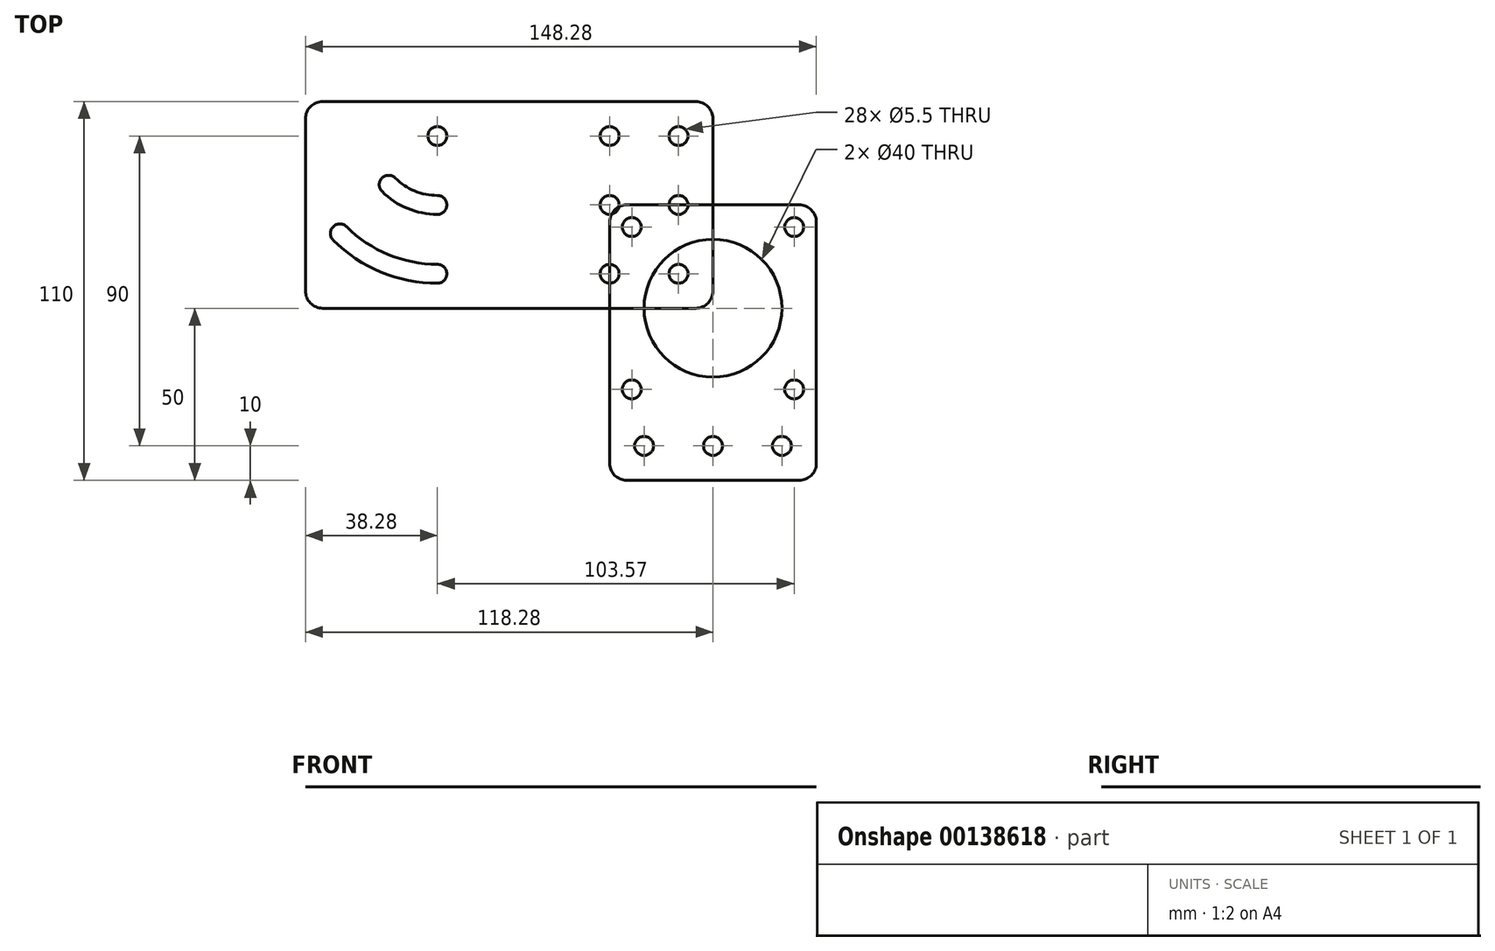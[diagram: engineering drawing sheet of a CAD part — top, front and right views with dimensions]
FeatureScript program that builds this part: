
annotation { "Feature Type Name" : "Feature", "Feature Type Description" : "" }
export const myFeature = defineFeature(function(context is Context, id is Id, definition is map)
    precondition{}
    {
        {
            var Q0;
            Q0=qCreatedBy(makeId("Top.planeOp"),FACE);
            var sketch = newSketch(context, id + "F0", { "sketchPlane" : qUnion([Q0])});
            skCircle(sketch, "E0", {"center": v(0, 0) * mm, "radius": 20 * mm});
            skLineSegment(sketch, "E1", {"start": v(-30, -30) * mm, "end": v(30, -30) * mm, "construction": true});
            skLineSegment(sketch, "E2", {"start": v(30, -30) * mm, "end": v(30, 25) * mm});
            skPoint(sketch, "E3", {"position": v(30, 0) * mm});
            skPoint(sketch, "E4", {"position": v(0, -30) * mm});
            skLineSegment(sketch, "E5", {"start": v(-30, 0) * mm, "end": v(30, 0) * mm, "construction": true});
            skLineSegment(sketch, "E6", {"start": v(0, 30) * mm, "end": v(0, -30) * mm, "construction": true});
            skLineSegment(sketch, "E7", {"start": v(25, 30) * mm, "end": v(-25, 30) * mm});
            skLineSegment(sketch, "E8", {"start": v(-30, 25) * mm, "end": v(-30, -30) * mm});
            skLineSegment(sketch, "E9", {"start": v(-23.57, 23.57) * mm, "end": v(23.57, 23.57) * mm, "construction": true});
            skPoint(sketch, "E10", {"position": v(0, 23.57) * mm});
            skLineSegment(sketch, "E11", {"start": v(23.57, 23.57) * mm, "end": v(23.57, -23.57) * mm, "construction": true});
            skPoint(sketch, "E12", {"position": v(23.57, 0) * mm});
            skLineSegment(sketch, "E13", {"start": v(-23.57, 23.57) * mm, "end": v(-23.57, -23.57) * mm, "construction": true});
            skLineSegment(sketch, "E14", {"start": v(-23.57, -23.57) * mm, "end": v(23.57, -23.57) * mm, "construction": true});
            skCircle(sketch, "E15", {"center": v(-23.57, 23.57) * mm, "radius": 2.75 * mm});
            skCircle(sketch, "E16", {"center": v(23.57, 23.57) * mm, "radius": 2.75 * mm});
            skCircle(sketch, "E17", {"center": v(-23.57, -23.57) * mm, "radius": 2.75 * mm});
            skCircle(sketch, "E18", {"center": v(23.57, -23.57) * mm, "radius": 2.75 * mm});
            skLineSegment(sketch, "E19", {"start": v(-30, -30) * mm, "end": v(-30, -45) * mm});
            skLineSegment(sketch, "E20", {"start": v(-25, -50) * mm, "end": v(25, -50) * mm});
            skLineSegment(sketch, "E21", {"start": v(30, -45) * mm, "end": v(30, -30) * mm});
            skLineSegment(sketch, "E22", {"start": v(-30, -40) * mm, "end": v(30, -40) * mm, "construction": true});
            skLineSegment(sketch, "E23", {"start": v(0, -30) * mm, "end": v(0, -50) * mm, "construction": true});
            skPoint(sketch, "E24", {"position": v(0, -40) * mm});
            skPoint(sketch, "E25", {"position": v(-20, -40) * mm});
            skPoint(sketch, "E26", {"position": v(20, -40) * mm});
            skCircle(sketch, "E27", {"center": v(-20, -40) * mm, "radius": 2.75 * mm});
            skCircle(sketch, "E28", {"center": v(0, -40) * mm, "radius": 2.75 * mm});
            skCircle(sketch, "E29", {"center": v(20, -40) * mm, "radius": 2.75 * mm});
            skPoint(sketch, "E30.visualSharp", {"position": v(-30, 30) * mm});
            skArc(sketch, "E30.filletArc", {"start": v(-25, 30) * mm, "mid": v(-28.54, 28.54) * mm, "end": v(-30, 25) * mm});
            skPoint(sketch, "E31.visualSharp", {"position": v(-30, -50) * mm});
            skArc(sketch, "E31.filletArc", {"start": v(-30, -45) * mm, "mid": v(-28.54, -48.54) * mm, "end": v(-25, -50) * mm});
            skPoint(sketch, "E32.visualSharp", {"position": v(30, -50) * mm});
            skArc(sketch, "E32.filletArc", {"start": v(25, -50) * mm, "mid": v(28.54, -48.54) * mm, "end": v(30, -45) * mm});
            skPoint(sketch, "E33.visualSharp", {"position": v(30, 30) * mm});
            skArc(sketch, "E33.filletArc", {"start": v(30, 25) * mm, "mid": v(28.54, 28.54) * mm, "end": v(25, 30) * mm});
            skSolve(sketch);
        }
        {
            var Q0;
            Q0=makeQuery(id+"F0.imprint","IMPRINT",FACE,{"disambiguationData":[TD([[makeQuery(id+"F0.imprint","IMPRINT",EDGE,{"derivedFrom":sQuery(id+"F0.wireOp",EDGE,"E0")}),-1.0]])]});
            extrude(context, id + "F1", {"entities" : qUnion([Q0]), "depth" : 1 / 203.2 * mm});
        }
        {
            var Q0;
            Q0=qCreatedBy(makeId("Top.planeOp"),FACE);
            var sketch = newSketch(context, id + "F2", { "sketchPlane" : qUnion([Q0])});
            skLineSegment(sketch, "E34.bottom", {"start": v(-5, 0) * mm, "end": v(-113.28, 0) * mm});
            skLineSegment(sketch, "E34.top", {"start": v(-5, 60) * mm, "end": v(-113.28, 60) * mm});
            skLineSegment(sketch, "E34.left", {"start": v(0, 5) * mm, "end": v(0, 55) * mm});
            skLineSegment(sketch, "E34.right", {"start": v(-118.28, 5) * mm, "end": v(-118.28, 55) * mm});
            skLineSegment(sketch, "E35", {"start": v(-118.28, 30) * mm, "end": v(0, 30) * mm, "construction": true});
            skLineSegment(sketch, "E36", {"start": v(-10, 60) * mm, "end": v(-10, 0) * mm, "construction": true});
            skLineSegment(sketch, "E37", {"start": v(0, 50) * mm, "end": v(-80, 50) * mm, "construction": true});
            skLineSegment(sketch, "E38", {"start": v(-80, 60) * mm, "end": v(-80, 0) * mm, "construction": true});
            skLineSegment(sketch, "E39", {"start": v(0, 10) * mm, "end": v(-80, 10) * mm, "construction": true});
            skLineSegment(sketch, "E40", {"start": v(-80, 50) * mm, "end": v(-110.23, 19.77) * mm, "construction": true});
            skArc(sketch, "E41", {"start": v(-94.14, 35.86) * mm, "mid": v(-87.65, 31.52) * mm, "end": v(-80, 30) * mm, "construction": true});
            skArc(sketch, "E42", {"start": v(-108.28, 21.72) * mm, "mid": v(-95.3, 13.04) * mm, "end": v(-80, 10) * mm, "construction": true});
            skCircle(sketch, "E43", {"center": v(-10, 50) * mm, "radius": 2.75 * mm});
            skCircle(sketch, "E44", {"center": v(-10, 30) * mm, "radius": 2.75 * mm});
            skCircle(sketch, "E45", {"center": v(-10, 10) * mm, "radius": 2.75 * mm});
            skLineSegment(sketch, "E46", {"start": v(-30, 60) * mm, "end": v(-30, 0) * mm, "construction": true});
            skCircle(sketch, "E47", {"center": v(-30, 10) * mm, "radius": 2.75 * mm});
            skCircle(sketch, "E48", {"center": v(-30, 30) * mm, "radius": 2.75 * mm});
            skCircle(sketch, "E49", {"center": v(-30, 50) * mm, "radius": 2.75 * mm});
            skCircle(sketch, "E50", {"center": v(-80, 50) * mm, "radius": 2.75 * mm});
            skArc(sketch, "E51", {"start": v(-92.2, 37.8) * mm, "mid": v(-86.6, 34.06) * mm, "end": v(-80, 32.75) * mm});
            skArc(sketch, "E52", {"start": v(-96.09, 33.91) * mm, "mid": v(-88.7, 28.98) * mm, "end": v(-80, 27.25) * mm});
            skArc(sketch, "E53", {"start": v(-106.34, 23.66) * mm, "mid": v(-94.25, 15.59) * mm, "end": v(-80, 12.75) * mm});
            skArc(sketch, "E54", {"start": v(-110.23, 19.77) * mm, "mid": v(-96.36, 10.5) * mm, "end": v(-80, 7.25) * mm});
            skArc(sketch, "E55", {"start": v(-80, 27.25) * mm, "mid": v(-77.25, 30) * mm, "end": v(-80, 32.75) * mm});
            skArc(sketch, "E56", {"start": v(-80, 7.25) * mm, "mid": v(-77.25, 10) * mm, "end": v(-80, 12.75) * mm});
            skArc(sketch, "E57", {"start": v(-106.34, 23.66) * mm, "mid": v(-110.23, 23.66) * mm, "end": v(-110.23, 19.77) * mm});
            skArc(sketch, "E58", {"start": v(-92.2, 37.8) * mm, "mid": v(-96.09, 37.8) * mm, "end": v(-96.09, 33.91) * mm});
            skPoint(sketch, "E59.visualSharp", {"position": v(0, 60) * mm});
            skArc(sketch, "E59.filletArc", {"start": v(0, 55) * mm, "mid": v(-1.46, 58.54) * mm, "end": v(-5, 60) * mm});
            skPoint(sketch, "E60.visualSharp", {"position": v(0, 0) * mm});
            skArc(sketch, "E60.filletArc", {"start": v(-5, 0) * mm, "mid": v(-1.46, 1.46) * mm, "end": v(0, 5) * mm});
            skPoint(sketch, "E61.visualSharp", {"position": v(-118.28, 0) * mm});
            skArc(sketch, "E61.filletArc", {"start": v(-118.28, 5) * mm, "mid": v(-116.82, 1.46) * mm, "end": v(-113.28, 0) * mm});
            skPoint(sketch, "E62.visualSharp", {"position": v(-118.28, 60) * mm});
            skArc(sketch, "E62.filletArc", {"start": v(-113.28, 60) * mm, "mid": v(-116.82, 58.54) * mm, "end": v(-118.28, 55) * mm});
            skSolve(sketch);
        }
        {
            var Q0;
            Q0=makeQuery(id+"F2.imprint","IMPRINT",FACE,{"disambiguationData":[TD([[makeQuery(id+"F2.imprint","IMPRINT",EDGE,{"derivedFrom":sQuery(id+"F2.wireOp",EDGE,"E34.bottom")}),-1.0]])]});
            extrude(context, id + "F3", {"entities" : qUnion([Q0]), "depth" : 1 / 203.2 * mm});
        }
    });
